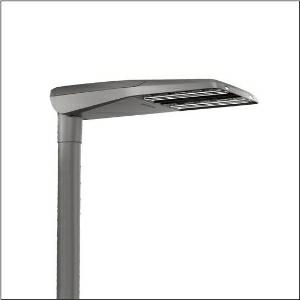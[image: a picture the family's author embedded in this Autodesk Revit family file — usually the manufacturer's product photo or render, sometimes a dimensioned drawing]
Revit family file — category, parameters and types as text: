
# Revit family: streetlight_sl_11_iq_midi___st1_2a_5xc3a31f08me_35e9
name_source: partatom
category: Lighting Fixtures
units: mm (PartAtom-declared; Revit-internal decimal feet)

## family parameters
Cut with Voids When Loaded = No
Host = Face
Light Source = No
Part Type = Normal
Room Calculation Point = No
Round Connector Dimension = Use Diameter
Shared = No

## types (1)
- --- (1 x LED, 15580 lm, 124.7 W, 3000K)
    Apparent Load = 125 VA
    CIE Flux Codes = 32 70 96 100 100
    Color Rendering = 80
    Color Temperature = 3000K
    Default Elevation = 1800 mm
    Description = Streetlight SL 11 iQ midi, mast luminaire, primary light control with 3 zone facetted reflector, of plastic, silver coated, highly specular, primary optical cover: cover, of PMMA, transparent, light distribution: ST1.2a, light emission: direct distribution, primary light characteristic: asymmetric, installation type: post-top, side-entry, lamps: LED, High Power LED, rated values: 15.580lm | 124,7W | 124,9lm/W (begin service life); end service life: 15.580lm | 132,2W; at 50% lumin. flux: 7.790lm | 57,1W | 136,4lm/W, colour temperature: 3000K, colour rendering: CRI > 80, light colour: 830, light setting 1 begin service life: 100% | 15.580lm | 124,7W | 124,9lm/W | 3.000K, light setting 1 end service life: 132,2W, further light settings possible, control: Street-Remote, optimised constant luminous flux control (CLO 2.0), Desk-Remote (wireless, voltage-free reading and setting of iQ features in the workshop via application-optimized NFC function/RFID function), Light-Fading, Smart-Wire, Night-Set, Lumen-Switch, Temp-Guard, Auto-Match, with cable H07RN-F 3x 1.5mm², mains connection: 230..240V, AC, 50/60Hz, connection cable pre-assembled, cable length: 12,5m, luminaire housing, of diecast aluminium, powder-coated, SITECO metallic grey (DB 702S), please order mast flange separately, inclination adjustable without tools: 0°, 5°, 10°, 15° (post-top) | 0°, -5°, -10°, -15° (side-entry), sealing non-destructively replaceable, multi-level sealing system, length: 780mm, width: 376mm, height: 118mm, mast flange for spigot size: 42mm (side-entry): 5XC10008XM4, 60/48mm (side-entry/post-top): 5XC10108XM2, 76/60mm (side-entry/post-top): 5XC10108XM1, equipment: Power, protection rating (complete): IP66, insulation class (complete): insulation class II (safety insulation), certification: CE, ENEC, ENEC+, VDE, impact resistance: IK10, permissible operating ambient temperature for outdoor applications: -25..+50°C, standard-compliant lighting for roads and squares, Environmental Product Declaration (EPD) tested and certified by an independent institute, packaging unit: 1 piece

Light Distribution: ST1.2a
    Height = 118 mm
    Lamp = 1 x LED
    Lamp Light Flux = 15580 lm
    Lamp Power = 124.7 W
    Lamp count = 1
    Length = 780 mm
    Luminous efficacy = 125 lm/W
    Manufacturer = Siteco
    ModVariant = No
    Model = 5XC3A31F08ME
    Number of Poles = 1
    OnlyDefault = Yes
    Power Factor = 1
    Product Name = Streetlight SL 11 iQ midi | ST1.2a
    Product group = mast luminaire | pylon top
    ProductGroupID = 6100
    Protection Class = Protection class II
    Protection Degree = IP 66
    RLX_Detail_Level = 1
    RLX_Emergency_Light_Flux = 0 lm
    RLX_Emergency_Type = 0
    RLX_Emergency_Type_DB = No
    RlxData = <blob elided: 70969 chars, md5=e10fb835>
    Socket = socket
    Standby Power = 0 W
    System Light Flux = 15580 lm
    System Power = 125 W
    Type Comments = factory setting: luminous flux: 100 % | dim-lin: 254 | 557 mA
    Type Image = l_1005960.jpg
    URL = http://relux.com
    VarID = @adj_193649
    Voltage = 0 V
    Weight = 0.00 kg
    Width = 376 mm

## geometry (parser evidence)
native form markers: Blend x4, Sweep x10
no freeform markers — native parametric forms only
